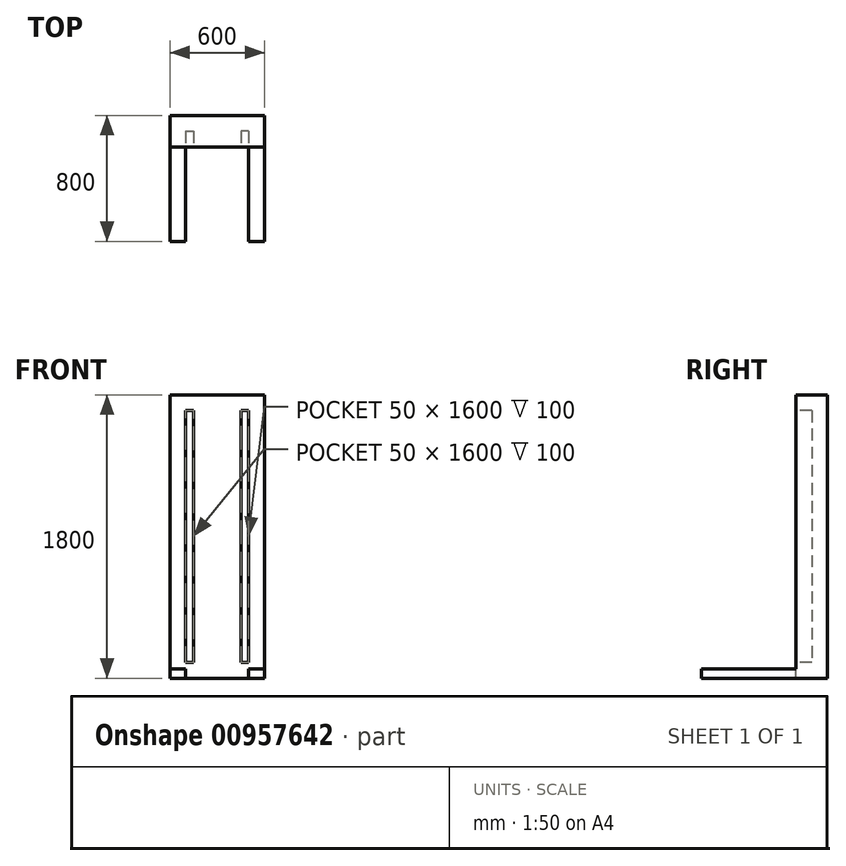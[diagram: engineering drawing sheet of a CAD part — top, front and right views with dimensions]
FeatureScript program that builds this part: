
annotation { "Feature Type Name" : "Feature", "Feature Type Description" : "" }
export const myFeature = defineFeature(function(context is Context, id is Id, definition is map)
    precondition{}
    {
        {
            var Q0;
            Q0=qCreatedBy(makeId("Front.planeOp"),FACE);
            var sketch = newSketch(context, id + "F0", { "sketchPlane" : qUnion([Q0])});
            skLineSegment(sketch, "E0", {"start": v(0, 0) * mm, "end": v(600, 0) * mm});
            skLineSegment(sketch, "E1", {"start": v(600, 0) * mm, "end": v(600, 1800) * mm});
            skLineSegment(sketch, "E2", {"start": v(600, 1800) * mm, "end": v(0, 1800) * mm});
            skLineSegment(sketch, "E3", {"start": v(0, 1800) * mm, "end": v(0, 0) * mm});
            skSolve(sketch);
        }
        {
            var Q0;
            Q0 = qSketchRegion(id + "F0", true);
            extrude(context, id + "F1", {"entities" : qUnion([Q0]), "depth" : 200 * mm, "offsetDistance" : 25 * mm});
        }
        {
            var Q0;
            Q0=makeQuery(id+"F1.opExtrude","CAP_FACE",FACE,{"disambiguationData":[OSD([sQuery(id+"F0.wireOp",EDGE,"E0"),sQuery(id+"F0.wireOp",EDGE,"E1"),sQuery(id+"F0.wireOp",EDGE,"E2"),sQuery(id+"F0.wireOp",EDGE,"E3")])],"isStart":false});
            var sketch = newSketch(context, id + "F2", { "sketchPlane" : qUnion([Q0])});
            skLineSegment(sketch, "E4.bottom", {"start": v(0, 0) * mm, "end": v(100, 0) * mm});
            skLineSegment(sketch, "E4.top", {"start": v(0, 60) * mm, "end": v(100, 60) * mm});
            skLineSegment(sketch, "E4.left", {"start": v(0, 0) * mm, "end": v(0, 60) * mm});
            skLineSegment(sketch, "E4.right", {"start": v(100, 0) * mm, "end": v(100, 60) * mm});
            skLineSegment(sketch, "E5", {"start": v(300, 1800) * mm, "end": v(300, 0) * mm});
            skLineSegment(sketch, "E6.MirrorCS", {"start": v(600, 60) * mm, "end": v(500, 60) * mm});
            skLineSegment(sketch, "E7.MirrorCS", {"start": v(600, 0) * mm, "end": v(600, 60) * mm});
            skLineSegment(sketch, "E8.MirrorCS", {"start": v(600, 0) * mm, "end": v(500, 0) * mm});
            skLineSegment(sketch, "E9.MirrorCS", {"start": v(500, 0) * mm, "end": v(500, 60) * mm});
            skSolve(sketch);
        }
        {
            var Q0;
            Q0 = qSketchRegion(id + "F2", true);
            extrude(context, id + "F3", {"entities" : qUnion([Q0]), "operationType" : NewBodyOperationType.ADD, "depth" : 600 * mm, "offsetDistance" : 25 * mm});
        }
        {
            var Q0;
            Q0=makeQuery(id+"F1.opExtrude","CAP_FACE",FACE,{"disambiguationData":[OSD([sQuery(id+"F0.wireOp",EDGE,"E0"),sQuery(id+"F0.wireOp",EDGE,"E1"),sQuery(id+"F0.wireOp",EDGE,"E2"),sQuery(id+"F0.wireOp",EDGE,"E3")])],"isStart":false});
            var sketch = newSketch(context, id + "F4", { "sketchPlane" : qUnion([Q0])});
            skLineSegment(sketch, "E10.bottom", {"start": v(100, 1700) * mm, "end": v(150, 1700) * mm});
            skLineSegment(sketch, "E10.top", {"start": v(100, 100) * mm, "end": v(150, 100) * mm});
            skLineSegment(sketch, "E10.left", {"start": v(100, 1700) * mm, "end": v(100, 100) * mm});
            skLineSegment(sketch, "E10.right", {"start": v(150, 1700) * mm, "end": v(150, 100) * mm});
            skLineSegment(sketch, "E11", {"start": v(300, 1800) * mm, "end": v(300, 1556.18) * mm});
            skLineSegment(sketch, "E12.MirrorCS", {"start": v(450, 1700) * mm, "end": v(450, 100) * mm});
            skLineSegment(sketch, "E13.MirrorCS", {"start": v(500, 1700) * mm, "end": v(500, 100) * mm});
            skLineSegment(sketch, "E14.MirrorCS", {"start": v(500, 1700) * mm, "end": v(450, 1700) * mm});
            skLineSegment(sketch, "E15.MirrorCS", {"start": v(500, 100) * mm, "end": v(450, 100) * mm});
            skSolve(sketch);
        }
        {
            var Q0;
            Q0 = qSketchRegion(id + "F4", true);
            extrude(context, id + "F5", {"entities" : qUnion([Q0]), "operationType" : NewBodyOperationType.REMOVE, "oppositeDirection" : true, "depth" : 100 * mm, "offsetDistance" : 25 * mm});
        }
    });
